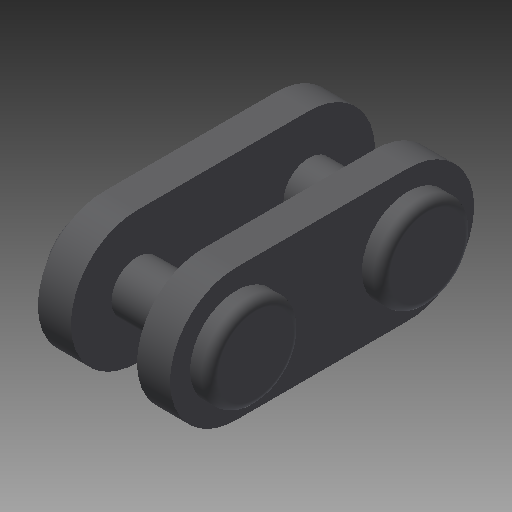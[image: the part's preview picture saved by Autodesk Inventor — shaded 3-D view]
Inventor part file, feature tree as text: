
AUTODESK INVENTOR PART (.ipt)
format: ipt  version: 2018 (Build 220112000, 112)  size: 188,928 bytes
history: native  units: mm
features: other x14, sketch x5, extrude x3, revolve x2
ambient origin geometry x8: Origin, YZ Plane, XZ Plane, XY Plane, X Axis, Y Axis, Z Axis, Center Point
bodies: Solid1 (feature_tree)
feature tree (24):
  extrude  "Extrusion1"  TaperAngle=360.0deg  [1 undecoded]
  revolve  "Revolution1"  [1 undecoded]
  revolve  "Revolution2"  [1 undecoded]
  extrude  "Extrusion2"  [1 undecoded]
  extrude  "Extrusion3"  [1 undecoded]
  other  "ZS1_XY"
  other  "ZS1_YZ"
  other  "ZS1_ZX"
  other  "ZS1_X"
  other  "ZS1_Y"
  other  "ZS1_Z"
  other  "ZS1_Center"
  other  "ZS2_XY"
  other  "ZS2_YZ"
  other  "ZS2_ZX"
  other  "ZS2_X"
  other  "ZS2_Y"
  other  "ZS2_Z"
  other  "ZS2_Center"
  sketch  "Skizze_1"  dims[d0=8.0mm d1=0.0mm d2=360.0deg]
  sketch  "Skizze_2"  dims[d3=360.0deg d4=8.0mm d5=0.0mm]
  sketch  "Skizze_3"  dims[d6=20.0mm d7=0.0mm]
  sketch  "Skizze_4"
  sketch  "Skizze_5"
note: 5 required parameter values undecoded (feature->parameter linkage not recoverable at this tier; creation-order binding heuristic only, values carry confidence <= 0.55)